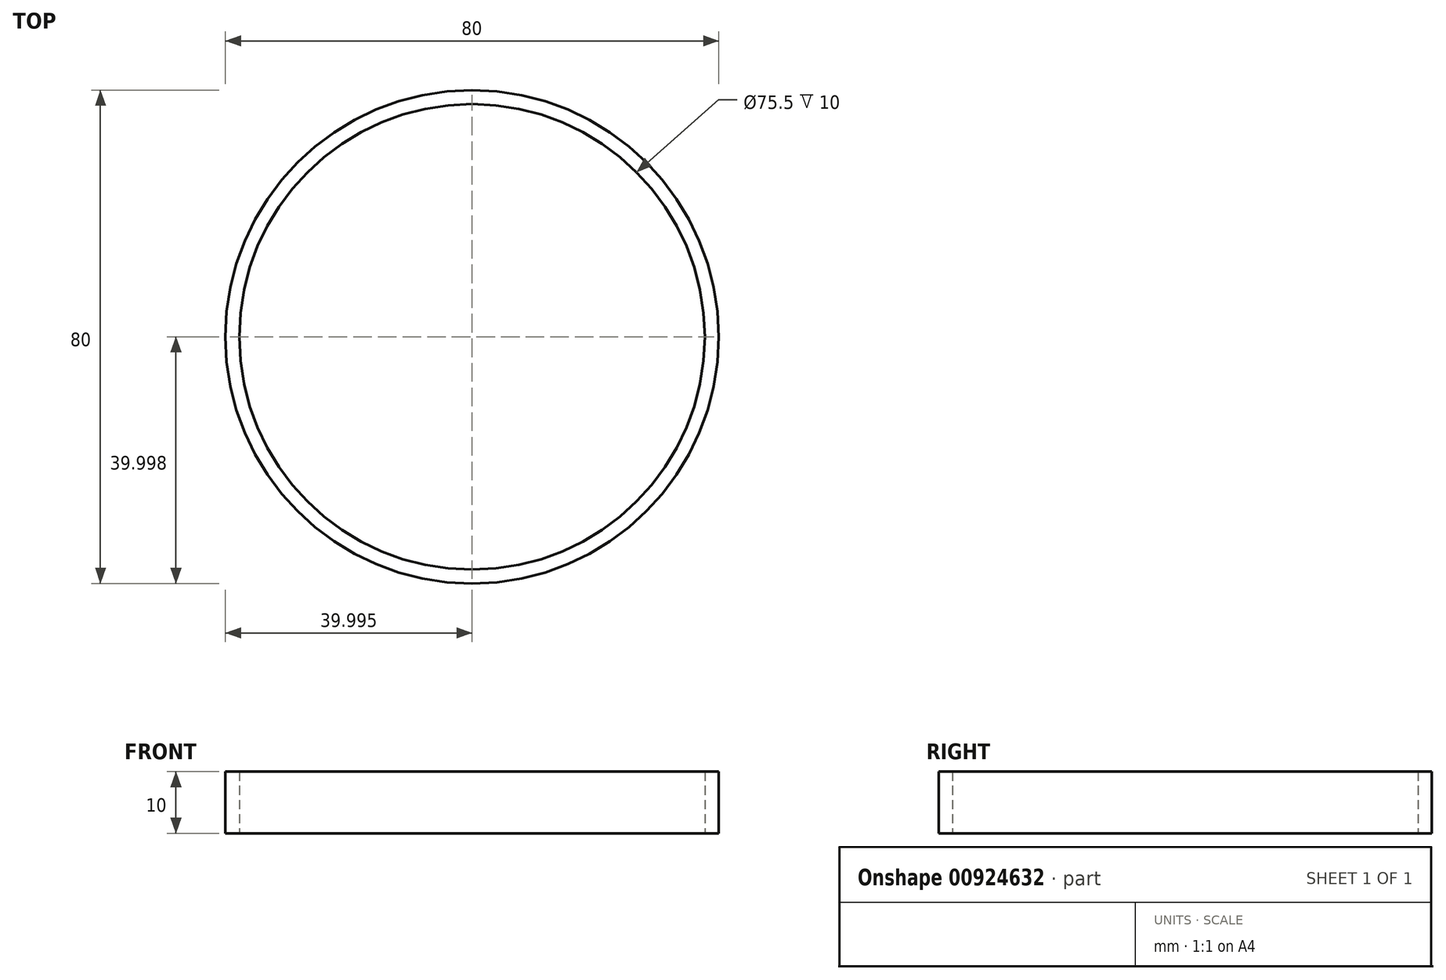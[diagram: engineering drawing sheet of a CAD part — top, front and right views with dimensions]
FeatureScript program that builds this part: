
annotation { "Feature Type Name" : "Feature", "Feature Type Description" : "" }
export const myFeature = defineFeature(function(context is Context, id is Id, definition is map)
    precondition{}
    {
        {
            var Q0;
            Q0=qCreatedBy(makeId("Top.planeOp"),FACE);
            var sketch = newSketch(context, id + "F0", { "sketchPlane" : qUnion([Q0])});
            skCircle(sketch, "E0", {"center": v(-120.12, -19.03) * mm, "radius": 37.75 * mm});
            skCircle(sketch, "E1", {"center": v(-120.12, -19.03) * mm, "radius": 40 * mm});
            skSolve(sketch);
        }
        {
            var Q0;
            Q0 = qSketchRegion(id + "F0", true);
            extrude(context, id + "F1", {"entities" : qUnion([Q0]), "depth" : 10 * mm, "offsetDistance" : 25 * mm});
        }
    });
